# Revit family: Chair-Soft_Seating-Allermuir-A820-Lola-Swivel_Base
name_source: partatom
category: Furniture
revit_build: Autodesk Revit MEP 2012 (Build: 20110309_2315(x64)
units: mm (PartAtom-declared; Revit-internal decimal feet)

## types (1)
- Lola-A820-Swivel_Base
    04 CSI = 12 51 00
    95 CSI = 12510
    Assembly Code = E2020200
    Back Rest = Fabric - Allermuir - Silcoates
    Base = Metal - Allermuir - Chrome - Polished
    Brochure URL = http://www.allermuir.net
    CAD Blocks URL = http://www.allermuir.net
    Color Availability = See price list for material options
    Fabric Spec Sheets = http://www.allermuir.net
    LEED Stats URL = http://www.allermuir.net
    Leg Base Height = 13"
    Manufacturer = Allermuir
    Manufacturer Fax = (419) 887 5805
    Model = A820
    Overall Depth = 26"
    Overall Height = 14"
    Overall Width = 30"
    Plugin Data URL = http://products.ecoscorecard.com
    Pricing URL = http://www.allermuir.net
    Product Line = Lola
    Product Page URL = http://www.allermuir.net
    Seat = Fabric - Allermuir - Silcoates
    Seat Height = 17"
    Specifications URL = http://www.allermuir.net
    Subcategory = Soft Seating
    URL = http://www.allermuir.net
    Weight = 0.0 lb
    White Plastic Back Membrane = No
    ecoScorecard Product Page = http://products.ecoscorecard.com
    ecoScorecard_data = http://thesenatorgroup.ecoscorecard.com

## geometry (parser evidence)
native form markers: Blend x9, Sweep x5
no freeform markers — native parametric forms only
